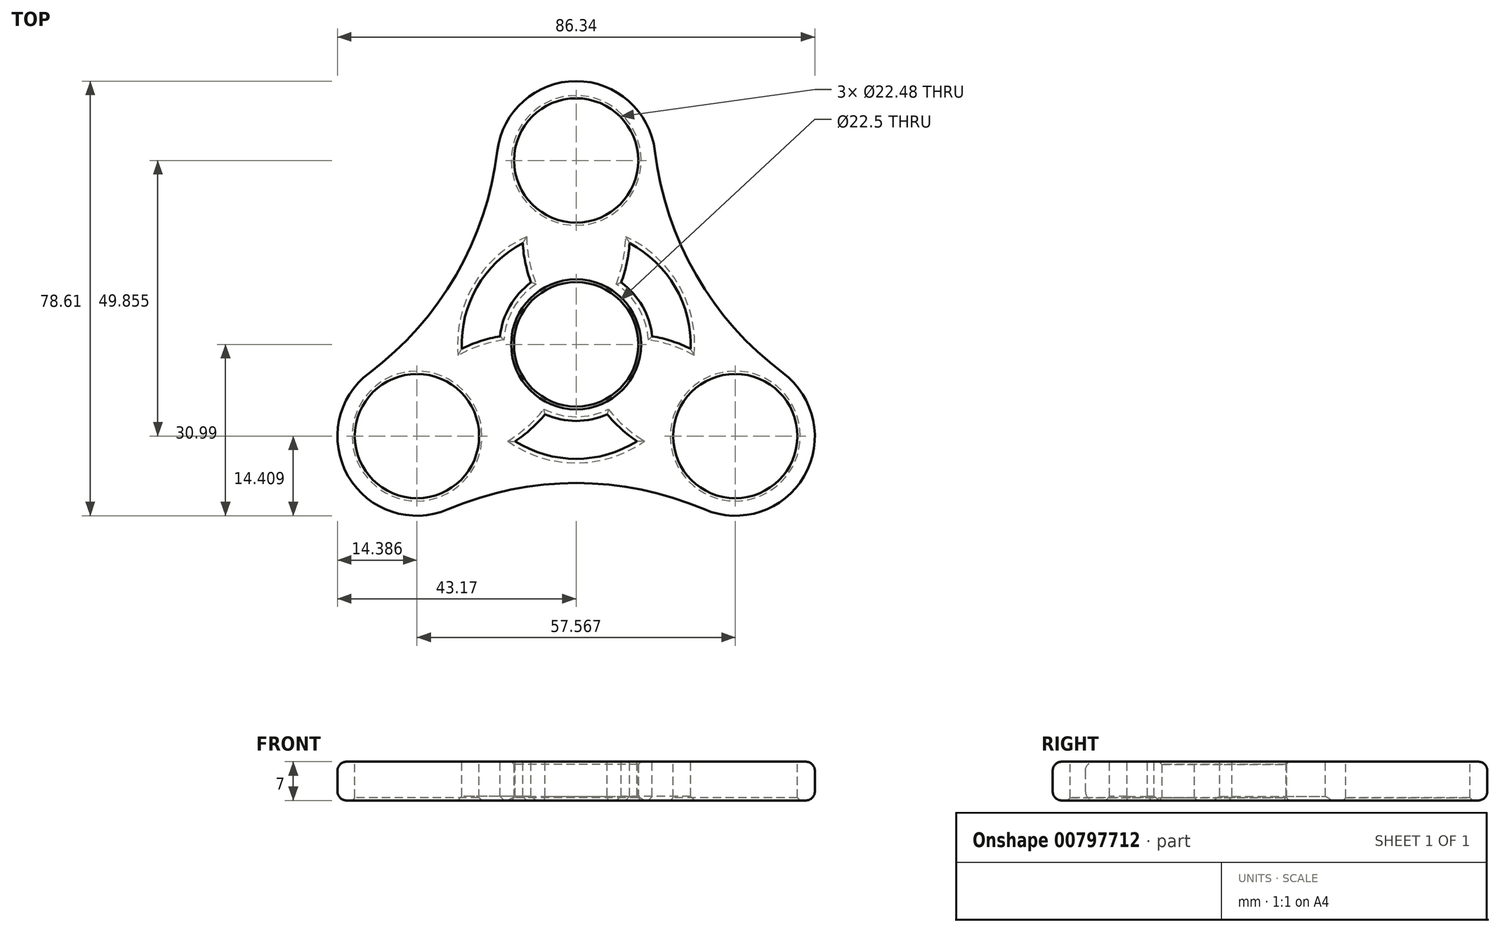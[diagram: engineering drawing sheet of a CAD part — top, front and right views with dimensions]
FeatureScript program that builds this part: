
annotation { "Feature Type Name" : "Feature", "Feature Type Description" : "" }
export const myFeature = defineFeature(function(context is Context, id is Id, definition is map)
    precondition{}
    {
        {
            var Q0;
            Q0=qCreatedBy(makeId("Top.planeOp"),FACE);
            var sketch = newSketch(context, id + "F0", { "sketchPlane" : qUnion([Q0])});
            skCircle(sketch, "E0", {"center": v(0, 0) * mm, "radius": 47.63 * mm, "construction": true});
            skLineSegment(sketch, "E1", {"start": v(0, 0) * mm, "end": v(-30.82, -17.8) * mm, "construction": true});
            skLineSegment(sketch, "E2", {"start": v(0, 0) * mm, "end": v(35.83, -20.69) * mm, "construction": true});
            skLineSegment(sketch, "E3", {"start": v(0, 0) * mm, "end": v(0, 29.12) * mm, "construction": true});
            skCircle(sketch, "E4", {"center": v(0, 0) * mm, "radius": 11.25 * mm});
            skArc(sketch, "E5", {"start": v(14.25, 34.97) * mm, "mid": v(0, 47.62) * mm, "end": v(-14.25, 34.97) * mm});
            skArc(sketch, "E6.1.0", {"start": v(-37.41, -5.15) * mm, "mid": v(-41.25, -23.82) * mm, "end": v(-23.16, -29.83) * mm});
            skArc(sketch, "E6.2.0", {"start": v(23.16, -29.83) * mm, "mid": v(41.25, -23.82) * mm, "end": v(37.41, -5.15) * mm});
            skArc(sketch, "E7", {"start": v(-37.41, -5.15) * mm, "mid": v(-21.71, 12.53) * mm, "end": v(-14.25, 34.97) * mm});
            skArc(sketch, "E8.1.0", {"start": v(23.16, -29.83) * mm, "mid": v(0, -25.08) * mm, "end": v(-23.16, -29.83) * mm});
            skArc(sketch, "E8.2.0", {"start": v(14.25, 34.97) * mm, "mid": v(21.71, 12.53) * mm, "end": v(37.41, -5.15) * mm});
            skSolve(sketch);
        }
        {
            var Q0;
            Q0 = qSketchRegion(id + "F0", true);
            extrude(context, id + "F1", {"entities" : qUnion([Q0]), "depth" : 7 * mm, "offsetDistance" : 25.4 * mm});
        }
        {
            var Q0;
            Q0=makeQuery(id+"F1.opExtrude","CAP_FACE",FACE,{"disambiguationData":[OSD([sQuery(id+"F0.wireOp",EDGE,"E4"),sQuery(id+"F0.wireOp",EDGE,"E5"),sQuery(id+"F0.wireOp",EDGE,"E6.1.0"),sQuery(id+"F0.wireOp",EDGE,"E6.2.0"),sQuery(id+"F0.wireOp",EDGE,"E7"),sQuery(id+"F0.wireOp",EDGE,"E8.1.0"),sQuery(id+"F0.wireOp",EDGE,"E8.2.0")])],"isStart":false});
            var sketch = newSketch(context, id + "F2", { "sketchPlane" : qUnion([Q0])});
            skCircle(sketch, "E9", {"center": v(0, 33.27) * mm, "radius": 11.24 * mm});
            skCircle(sketch, "E10.1.0", {"center": v(-28.78, -16.58) * mm, "radius": 11.24 * mm});
            skCircle(sketch, "E10.2.0", {"center": v(28.78, -16.58) * mm, "radius": 11.24 * mm});
            skPoint(sketch, "E10.center", {"position": v(0, 0.04) * mm});
            skSolve(sketch);
        }
        {
            var Q0;
            Q0 = qSketchRegion(id + "F2", true);
            extrude(context, id + "F3", {"entities" : qUnion([Q0]), "operationType" : NewBodyOperationType.REMOVE, "endBound" : BoundingType.THROUGH_ALL, "oppositeDirection" : true, "depth" : 25.4 * mm, "offsetDistance" : 25.4 * mm});
        }
        {
            var Q0;
            Q0=makeQuery(id+"F1.opExtrude","CAP_FACE",FACE,{"disambiguationData":[OSD([sQuery(id+"F0.wireOp",EDGE,"E4"),sQuery(id+"F0.wireOp",EDGE,"E5"),sQuery(id+"F0.wireOp",EDGE,"E6.1.0"),sQuery(id+"F0.wireOp",EDGE,"E6.2.0"),sQuery(id+"F0.wireOp",EDGE,"E7"),sQuery(id+"F0.wireOp",EDGE,"E8.1.0"),sQuery(id+"F0.wireOp",EDGE,"E8.2.0")])],"isStart":false});
            var sketch = newSketch(context, id + "F4", { "sketchPlane" : qUnion([Q0])});
            skArc(sketch, "E11", {"start": v(-5.62, -12.65) * mm, "mid": v(0, -13.84) * mm, "end": v(5.62, -12.65) * mm});
            skArc(sketch, "E12", {"start": v(-11.02, -17.52) * mm, "mid": v(0, -20.7) * mm, "end": v(11.02, -17.52) * mm});
            skArc(sketch, "E13", {"start": v(-9.66, 18.3) * mm, "mid": v(-9.16, 14.7) * mm, "end": v(-8.15, 11.19) * mm});
            skArc(sketch, "E14", {"start": v(8.15, 11.19) * mm, "mid": v(9.16, 14.7) * mm, "end": v(9.66, 18.3) * mm});
            skArc(sketch, "E15.1.0", {"start": v(-11.02, -17.52) * mm, "mid": v(-8.14, -15.28) * mm, "end": v(-5.62, -12.65) * mm});
            skArc(sketch, "E15.1.1", {"start": v(-13.77, 1.46) * mm, "mid": v(-17.3, 0.59) * mm, "end": v(-20.69, -0.78) * mm});
            skArc(sketch, "E15.2.0", {"start": v(20.69, -0.78) * mm, "mid": v(17.3, 0.59) * mm, "end": v(13.77, 1.46) * mm});
            skArc(sketch, "E15.2.1", {"start": v(5.62, -12.65) * mm, "mid": v(8.14, -15.28) * mm, "end": v(11.02, -17.52) * mm});
            skArc(sketch, "E16.trimOffspring", {"start": v(-8.15, 11.19) * mm, "mid": v(-11.99, 6.92) * mm, "end": v(-13.77, 1.46) * mm});
            skArc(sketch, "E17.trimOffspring", {"start": v(-9.66, 18.3) * mm, "mid": v(-17.93, 10.35) * mm, "end": v(-20.69, -0.78) * mm});
            skArc(sketch, "E18.trimOffspring", {"start": v(20.69, -0.78) * mm, "mid": v(17.93, 10.35) * mm, "end": v(9.66, 18.3) * mm});
            skArc(sketch, "E19.trimOffspring", {"start": v(13.77, 1.46) * mm, "mid": v(11.99, 6.92) * mm, "end": v(8.15, 11.19) * mm});
            skLineSegment(sketch, "E20", {"start": v(0, 0) * mm, "end": v(-13.68, -7.9) * mm, "construction": true});
            skLineSegment(sketch, "E21.1.0", {"start": v(0, 0) * mm, "end": v(27.36, -15.8) * mm, "construction": true});
            skLineSegment(sketch, "E22.trimOffspring", {"start": v(-16.5, -9.52) * mm, "end": v(-27.36, -15.8) * mm, "construction": true});
            skSolve(sketch);
        }
        {
            var Q0;
            Q0 = qSketchRegion(id + "F4", true);
            extrude(context, id + "F5", {"entities" : qUnion([Q0]), "operationType" : NewBodyOperationType.REMOVE, "endBound" : BoundingType.THROUGH_ALL, "oppositeDirection" : true, "depth" : 25.4 * mm, "offsetDistance" : 25.4 * mm});
        }
        {
            var Q0;
            Q0=makeQuery(id+"F1.opExtrude","CAP_EDGE",EDGE,{"disambiguationData":[OSD([sQuery(id+"F0.wireOp",EDGE,"E8.1.0")])],"isStart":false});
            var Q1;
            Q1=makeQuery(id+"F1.opExtrude","CAP_EDGE",EDGE,{"disambiguationData":[OSD([sQuery(id+"F0.wireOp",EDGE,"E8.1.0")])],"isStart":true});
            fillet(context, id + "F6", {"entities" : qUnion([Q0, Q1]), "radius" : 1.62 * mm, "tangentPropagation" : true, "allowEdgeOverflow" : false});
        }
        {
            var Q0;
            Q0=makeQuery(id+"F5.boolean.opBoolean","COPY",EDGE,{"derivedFrom":makeQuery(id+"F5.opExtrude","CAP_EDGE",EDGE,{"disambiguationData":[OSD([sQuery(id+"F4.wireOp",EDGE,"E17.trimOffspring")])],"isStart":true})});
            var Q1;
            Q1=makeQuery(id+"F5.boolean.opBoolean","COPY",EDGE,{"derivedFrom":makeQuery(id+"F5.opExtrude","CAP_EDGE",EDGE,{"disambiguationData":[OSD([sQuery(id+"F4.wireOp",EDGE,"E13")])],"isStart":true})});
            var Q2;
            Q2=makeQuery(id+"F5.boolean.opBoolean","COPY",EDGE,{"derivedFrom":makeQuery(id+"F5.opExtrude","CAP_EDGE",EDGE,{"disambiguationData":[OSD([sQuery(id+"F4.wireOp",EDGE,"E16.trimOffspring")])],"isStart":true})});
            var Q3;
            Q3=makeQuery(id+"F5.boolean.opBoolean","COPY",EDGE,{"derivedFrom":makeQuery(id+"F5.opExtrude","CAP_EDGE",EDGE,{"disambiguationData":[OSD([sQuery(id+"F4.wireOp",EDGE,"E15.1.1")])],"isStart":true})});
            var Q4;
            Q4=makeQuery(id+"F5.boolean.opBoolean","COPY",EDGE,{"derivedFrom":makeQuery(id+"F5.opExtrude","CAP_EDGE",EDGE,{"disambiguationData":[OSD([sQuery(id+"F4.wireOp",EDGE,"E14")])],"isStart":true})});
            var Q5;
            Q5=makeQuery(id+"F5.boolean.opBoolean","COPY",EDGE,{"derivedFrom":makeQuery(id+"F5.opExtrude","CAP_EDGE",EDGE,{"disambiguationData":[OSD([sQuery(id+"F4.wireOp",EDGE,"E19.trimOffspring")])],"isStart":true})});
            var Q6;
            Q6=makeQuery(id+"F5.boolean.opBoolean","COPY",EDGE,{"derivedFrom":makeQuery(id+"F5.opExtrude","CAP_EDGE",EDGE,{"disambiguationData":[OSD([sQuery(id+"F4.wireOp",EDGE,"E15.2.0")])],"isStart":true})});
            var Q7;
            Q7=makeQuery(id+"F5.boolean.opBoolean","COPY",EDGE,{"derivedFrom":makeQuery(id+"F5.opExtrude","CAP_EDGE",EDGE,{"disambiguationData":[OSD([sQuery(id+"F4.wireOp",EDGE,"E18.trimOffspring")])],"isStart":true})});
            var Q8;
            Q8=makeQuery(id+"F5.boolean.opBoolean","COPY",EDGE,{"derivedFrom":makeQuery(id+"F5.opExtrude","CAP_EDGE",EDGE,{"disambiguationData":[OSD([sQuery(id+"F4.wireOp",EDGE,"E15.2.1")])],"isStart":true})});
            var Q9;
            Q9=makeQuery(id+"F5.boolean.opBoolean","COPY",EDGE,{"derivedFrom":makeQuery(id+"F5.opExtrude","CAP_EDGE",EDGE,{"disambiguationData":[OSD([sQuery(id+"F4.wireOp",EDGE,"E11")])],"isStart":true})});
            var Q10;
            Q10=makeQuery(id+"F5.boolean.opBoolean","COPY",EDGE,{"derivedFrom":makeQuery(id+"F5.opExtrude","CAP_EDGE",EDGE,{"disambiguationData":[OSD([sQuery(id+"F4.wireOp",EDGE,"E15.1.0")])],"isStart":true})});
            var Q11;
            Q11=makeQuery(id+"F5.boolean.opBoolean","COPY",EDGE,{"derivedFrom":makeQuery(id+"F5.opExtrude","CAP_EDGE",EDGE,{"disambiguationData":[OSD([sQuery(id+"F4.wireOp",EDGE,"E12")])],"isStart":true})});
            var Q12;
            Q12=makeQuery(id+"F5.boolean.opBoolean","INTERSECT",EDGE,{"derivedFrom":[makeQuery(id+"F1.opExtrude","CAP_FACE",FACE,{"disambiguationData":[OSD([sQuery(id+"F0.wireOp",EDGE,"E4"),sQuery(id+"F0.wireOp",EDGE,"E5"),sQuery(id+"F0.wireOp",EDGE,"E6.1.0"),sQuery(id+"F0.wireOp",EDGE,"E6.2.0"),sQuery(id+"F0.wireOp",EDGE,"E7"),sQuery(id+"F0.wireOp",EDGE,"E8.1.0"),sQuery(id+"F0.wireOp",EDGE,"E8.2.0")])],"isStart":true}),makeQuery(id+"F5.opExtrude","SWEPT_FACE",FACE,{"disambiguationData":[OSD([sQuery(id+"F4.wireOp",EDGE,"E12")])]})]});
            var Q13;
            Q13=makeQuery(id+"F5.boolean.opBoolean","INTERSECT",EDGE,{"derivedFrom":[makeQuery(id+"F1.opExtrude","CAP_FACE",FACE,{"disambiguationData":[OSD([sQuery(id+"F0.wireOp",EDGE,"E4"),sQuery(id+"F0.wireOp",EDGE,"E5"),sQuery(id+"F0.wireOp",EDGE,"E6.1.0"),sQuery(id+"F0.wireOp",EDGE,"E6.2.0"),sQuery(id+"F0.wireOp",EDGE,"E7"),sQuery(id+"F0.wireOp",EDGE,"E8.1.0"),sQuery(id+"F0.wireOp",EDGE,"E8.2.0")])],"isStart":true}),makeQuery(id+"F5.opExtrude","SWEPT_FACE",FACE,{"disambiguationData":[OSD([sQuery(id+"F4.wireOp",EDGE,"E11")])]})]});
            var Q14;
            Q14=makeQuery(id+"F5.boolean.opBoolean","INTERSECT",EDGE,{"derivedFrom":[makeQuery(id+"F1.opExtrude","CAP_FACE",FACE,{"disambiguationData":[OSD([sQuery(id+"F0.wireOp",EDGE,"E4"),sQuery(id+"F0.wireOp",EDGE,"E5"),sQuery(id+"F0.wireOp",EDGE,"E6.1.0"),sQuery(id+"F0.wireOp",EDGE,"E6.2.0"),sQuery(id+"F0.wireOp",EDGE,"E7"),sQuery(id+"F0.wireOp",EDGE,"E8.1.0"),sQuery(id+"F0.wireOp",EDGE,"E8.2.0")])],"isStart":true}),makeQuery(id+"F5.opExtrude","SWEPT_FACE",FACE,{"disambiguationData":[OSD([sQuery(id+"F4.wireOp",EDGE,"E15.1.0")])]})]});
            var Q15;
            Q15=makeQuery(id+"F5.boolean.opBoolean","INTERSECT",EDGE,{"derivedFrom":[makeQuery(id+"F1.opExtrude","CAP_FACE",FACE,{"disambiguationData":[OSD([sQuery(id+"F0.wireOp",EDGE,"E4"),sQuery(id+"F0.wireOp",EDGE,"E5"),sQuery(id+"F0.wireOp",EDGE,"E6.1.0"),sQuery(id+"F0.wireOp",EDGE,"E6.2.0"),sQuery(id+"F0.wireOp",EDGE,"E7"),sQuery(id+"F0.wireOp",EDGE,"E8.1.0"),sQuery(id+"F0.wireOp",EDGE,"E8.2.0")])],"isStart":true}),makeQuery(id+"F5.opExtrude","SWEPT_FACE",FACE,{"disambiguationData":[OSD([sQuery(id+"F4.wireOp",EDGE,"E15.2.1")])]})]});
            var Q16;
            Q16=makeQuery(id+"F5.boolean.opBoolean","INTERSECT",EDGE,{"derivedFrom":[makeQuery(id+"F1.opExtrude","CAP_FACE",FACE,{"disambiguationData":[OSD([sQuery(id+"F0.wireOp",EDGE,"E4"),sQuery(id+"F0.wireOp",EDGE,"E5"),sQuery(id+"F0.wireOp",EDGE,"E6.1.0"),sQuery(id+"F0.wireOp",EDGE,"E6.2.0"),sQuery(id+"F0.wireOp",EDGE,"E7"),sQuery(id+"F0.wireOp",EDGE,"E8.1.0"),sQuery(id+"F0.wireOp",EDGE,"E8.2.0")])],"isStart":true}),makeQuery(id+"F5.opExtrude","SWEPT_FACE",FACE,{"disambiguationData":[OSD([sQuery(id+"F4.wireOp",EDGE,"E15.2.0")])]})]});
            var Q17;
            Q17=makeQuery(id+"F5.boolean.opBoolean","INTERSECT",EDGE,{"derivedFrom":[makeQuery(id+"F1.opExtrude","CAP_FACE",FACE,{"disambiguationData":[OSD([sQuery(id+"F0.wireOp",EDGE,"E4"),sQuery(id+"F0.wireOp",EDGE,"E5"),sQuery(id+"F0.wireOp",EDGE,"E6.1.0"),sQuery(id+"F0.wireOp",EDGE,"E6.2.0"),sQuery(id+"F0.wireOp",EDGE,"E7"),sQuery(id+"F0.wireOp",EDGE,"E8.1.0"),sQuery(id+"F0.wireOp",EDGE,"E8.2.0")])],"isStart":true}),makeQuery(id+"F5.opExtrude","SWEPT_FACE",FACE,{"disambiguationData":[OSD([sQuery(id+"F4.wireOp",EDGE,"E18.trimOffspring")])]})]});
            var Q18;
            Q18=makeQuery(id+"F5.boolean.opBoolean","INTERSECT",EDGE,{"derivedFrom":[makeQuery(id+"F1.opExtrude","CAP_FACE",FACE,{"disambiguationData":[OSD([sQuery(id+"F0.wireOp",EDGE,"E4"),sQuery(id+"F0.wireOp",EDGE,"E5"),sQuery(id+"F0.wireOp",EDGE,"E6.1.0"),sQuery(id+"F0.wireOp",EDGE,"E6.2.0"),sQuery(id+"F0.wireOp",EDGE,"E7"),sQuery(id+"F0.wireOp",EDGE,"E8.1.0"),sQuery(id+"F0.wireOp",EDGE,"E8.2.0")])],"isStart":true}),makeQuery(id+"F5.opExtrude","SWEPT_FACE",FACE,{"disambiguationData":[OSD([sQuery(id+"F4.wireOp",EDGE,"E19.trimOffspring")])]})]});
            var Q19;
            Q19=makeQuery(id+"F5.boolean.opBoolean","INTERSECT",EDGE,{"derivedFrom":[makeQuery(id+"F1.opExtrude","CAP_FACE",FACE,{"disambiguationData":[OSD([sQuery(id+"F0.wireOp",EDGE,"E4"),sQuery(id+"F0.wireOp",EDGE,"E5"),sQuery(id+"F0.wireOp",EDGE,"E6.1.0"),sQuery(id+"F0.wireOp",EDGE,"E6.2.0"),sQuery(id+"F0.wireOp",EDGE,"E7"),sQuery(id+"F0.wireOp",EDGE,"E8.1.0"),sQuery(id+"F0.wireOp",EDGE,"E8.2.0")])],"isStart":true}),makeQuery(id+"F5.opExtrude","SWEPT_FACE",FACE,{"disambiguationData":[OSD([sQuery(id+"F4.wireOp",EDGE,"E14")])]})]});
            var Q20;
            Q20=makeQuery(id+"F5.boolean.opBoolean","INTERSECT",EDGE,{"derivedFrom":[makeQuery(id+"F1.opExtrude","CAP_FACE",FACE,{"disambiguationData":[OSD([sQuery(id+"F0.wireOp",EDGE,"E4"),sQuery(id+"F0.wireOp",EDGE,"E5"),sQuery(id+"F0.wireOp",EDGE,"E6.1.0"),sQuery(id+"F0.wireOp",EDGE,"E6.2.0"),sQuery(id+"F0.wireOp",EDGE,"E7"),sQuery(id+"F0.wireOp",EDGE,"E8.1.0"),sQuery(id+"F0.wireOp",EDGE,"E8.2.0")])],"isStart":true}),makeQuery(id+"F5.opExtrude","SWEPT_FACE",FACE,{"disambiguationData":[OSD([sQuery(id+"F4.wireOp",EDGE,"E13")])]})]});
            var Q21;
            Q21=makeQuery(id+"F5.boolean.opBoolean","INTERSECT",EDGE,{"derivedFrom":[makeQuery(id+"F1.opExtrude","CAP_FACE",FACE,{"disambiguationData":[OSD([sQuery(id+"F0.wireOp",EDGE,"E4"),sQuery(id+"F0.wireOp",EDGE,"E5"),sQuery(id+"F0.wireOp",EDGE,"E6.1.0"),sQuery(id+"F0.wireOp",EDGE,"E6.2.0"),sQuery(id+"F0.wireOp",EDGE,"E7"),sQuery(id+"F0.wireOp",EDGE,"E8.1.0"),sQuery(id+"F0.wireOp",EDGE,"E8.2.0")])],"isStart":true}),makeQuery(id+"F5.opExtrude","SWEPT_FACE",FACE,{"disambiguationData":[OSD([sQuery(id+"F4.wireOp",EDGE,"E17.trimOffspring")])]})]});
            var Q22;
            Q22=makeQuery(id+"F5.boolean.opBoolean","INTERSECT",EDGE,{"derivedFrom":[makeQuery(id+"F1.opExtrude","CAP_FACE",FACE,{"disambiguationData":[OSD([sQuery(id+"F0.wireOp",EDGE,"E4"),sQuery(id+"F0.wireOp",EDGE,"E5"),sQuery(id+"F0.wireOp",EDGE,"E6.1.0"),sQuery(id+"F0.wireOp",EDGE,"E6.2.0"),sQuery(id+"F0.wireOp",EDGE,"E7"),sQuery(id+"F0.wireOp",EDGE,"E8.1.0"),sQuery(id+"F0.wireOp",EDGE,"E8.2.0")])],"isStart":true}),makeQuery(id+"F5.opExtrude","SWEPT_FACE",FACE,{"disambiguationData":[OSD([sQuery(id+"F4.wireOp",EDGE,"E15.1.1")])]})]});
            var Q23;
            Q23=makeQuery(id+"F5.boolean.opBoolean","INTERSECT",EDGE,{"derivedFrom":[makeQuery(id+"F1.opExtrude","CAP_FACE",FACE,{"disambiguationData":[OSD([sQuery(id+"F0.wireOp",EDGE,"E4"),sQuery(id+"F0.wireOp",EDGE,"E5"),sQuery(id+"F0.wireOp",EDGE,"E6.1.0"),sQuery(id+"F0.wireOp",EDGE,"E6.2.0"),sQuery(id+"F0.wireOp",EDGE,"E7"),sQuery(id+"F0.wireOp",EDGE,"E8.1.0"),sQuery(id+"F0.wireOp",EDGE,"E8.2.0")])],"isStart":true}),makeQuery(id+"F5.opExtrude","SWEPT_FACE",FACE,{"disambiguationData":[OSD([sQuery(id+"F4.wireOp",EDGE,"E16.trimOffspring")])]})]});
            chamfer(context, id + "F7", {"entities" : qUnion([Q0, Q1, Q2, Q3, Q4, Q5, Q6, Q7, Q8, Q9, Q10, Q11, Q12, Q13, Q14, Q15, Q16, Q17, Q18, Q19, Q20, Q21, Q22, Q23]), "width" : .75 * mm, "tangentPropagation" : true});
        }
        {
            var Q0;
            Q0=makeQuery(id+"F3.boolean.opBoolean","COPY",EDGE,{"derivedFrom":makeQuery(id+"F3.opExtrude","CAP_EDGE",EDGE,{"disambiguationData":[OSD([sQuery(id+"F2.wireOp",EDGE,"E10.2.0")])],"isStart":true})});
            var Q1;
            Q1=makeQuery(id+"F3.boolean.opBoolean","COPY",EDGE,{"derivedFrom":makeQuery(id+"F3.opExtrude","CAP_EDGE",EDGE,{"disambiguationData":[OSD([sQuery(id+"F2.wireOp",EDGE,"E9")])],"isStart":true})});
            var Q2;
            Q2=makeQuery(id+"F3.boolean.opBoolean","COPY",EDGE,{"derivedFrom":makeQuery(id+"F3.opExtrude","CAP_EDGE",EDGE,{"disambiguationData":[OSD([sQuery(id+"F2.wireOp",EDGE,"E10.1.0")])],"isStart":true})});
            var Q3;
            Q3=makeQuery(id+"F1.opExtrude","CAP_EDGE",EDGE,{"disambiguationData":[OSD([sQuery(id+"F0.wireOp",EDGE,"E4")])],"isStart":false});
            var Q4;
            Q4=makeQuery(id+"F1.opExtrude","CAP_EDGE",EDGE,{"disambiguationData":[OSD([sQuery(id+"F0.wireOp",EDGE,"E4")])],"isStart":true});
            var Q5;
            Q5=makeQuery(id+"F3.boolean.opBoolean","INTERSECT",EDGE,{"derivedFrom":[makeQuery(id+"F1.opExtrude","CAP_FACE",FACE,{"disambiguationData":[OSD([sQuery(id+"F0.wireOp",EDGE,"E4"),sQuery(id+"F0.wireOp",EDGE,"E5"),sQuery(id+"F0.wireOp",EDGE,"E6.1.0"),sQuery(id+"F0.wireOp",EDGE,"E6.2.0"),sQuery(id+"F0.wireOp",EDGE,"E7"),sQuery(id+"F0.wireOp",EDGE,"E8.1.0"),sQuery(id+"F0.wireOp",EDGE,"E8.2.0")])],"isStart":true}),makeQuery(id+"F3.opExtrude","SWEPT_FACE",FACE,{"disambiguationData":[OSD([sQuery(id+"F2.wireOp",EDGE,"E10.1.0")])]})]});
            var Q6;
            Q6=makeQuery(id+"F3.boolean.opBoolean","INTERSECT",EDGE,{"derivedFrom":[makeQuery(id+"F1.opExtrude","CAP_FACE",FACE,{"disambiguationData":[OSD([sQuery(id+"F0.wireOp",EDGE,"E4"),sQuery(id+"F0.wireOp",EDGE,"E5"),sQuery(id+"F0.wireOp",EDGE,"E6.1.0"),sQuery(id+"F0.wireOp",EDGE,"E6.2.0"),sQuery(id+"F0.wireOp",EDGE,"E7"),sQuery(id+"F0.wireOp",EDGE,"E8.1.0"),sQuery(id+"F0.wireOp",EDGE,"E8.2.0")])],"isStart":true}),makeQuery(id+"F3.opExtrude","SWEPT_FACE",FACE,{"disambiguationData":[OSD([sQuery(id+"F2.wireOp",EDGE,"E9")])]})]});
            var Q7;
            Q7=makeQuery(id+"F3.boolean.opBoolean","INTERSECT",EDGE,{"derivedFrom":[makeQuery(id+"F1.opExtrude","CAP_FACE",FACE,{"disambiguationData":[OSD([sQuery(id+"F0.wireOp",EDGE,"E4"),sQuery(id+"F0.wireOp",EDGE,"E5"),sQuery(id+"F0.wireOp",EDGE,"E6.1.0"),sQuery(id+"F0.wireOp",EDGE,"E6.2.0"),sQuery(id+"F0.wireOp",EDGE,"E7"),sQuery(id+"F0.wireOp",EDGE,"E8.1.0"),sQuery(id+"F0.wireOp",EDGE,"E8.2.0")])],"isStart":true}),makeQuery(id+"F3.opExtrude","SWEPT_FACE",FACE,{"disambiguationData":[OSD([sQuery(id+"F2.wireOp",EDGE,"E10.2.0")])]})]});
            chamfer(context, id + "F8", {"entities" : qUnion([Q0, Q1, Q2, Q3, Q4, Q5, Q6, Q7]), "width" : .5 * mm, "tangentPropagation" : true});
        }
    });
